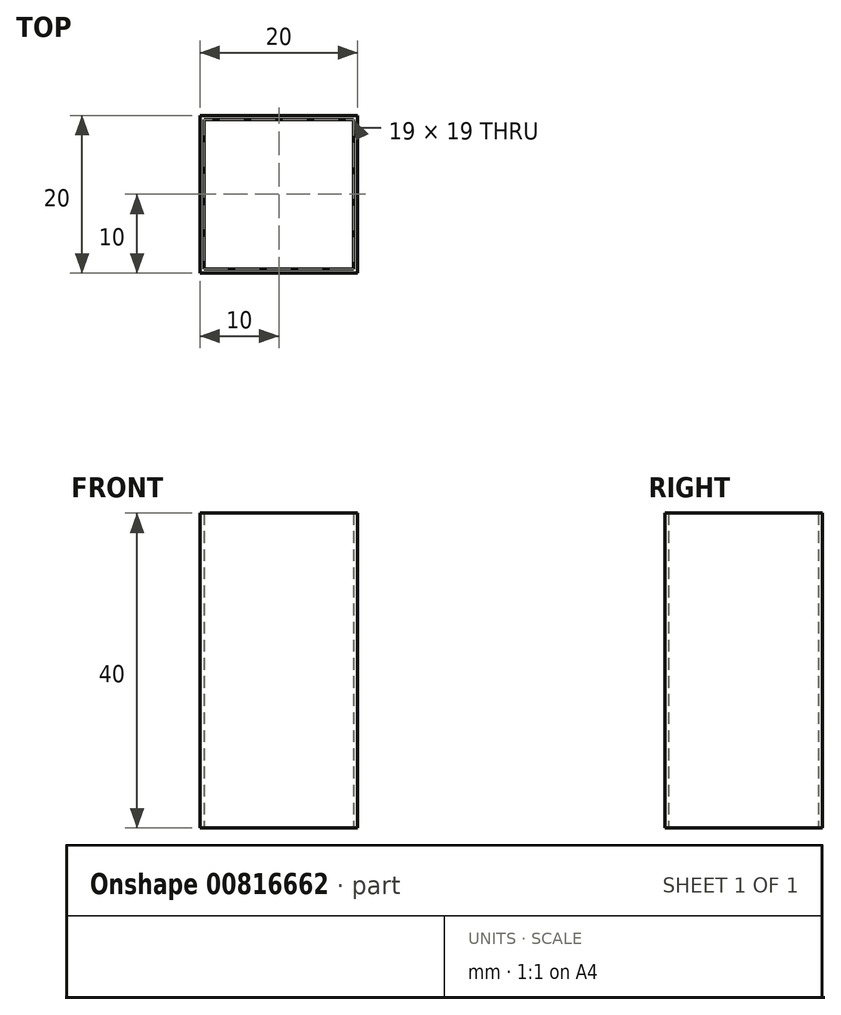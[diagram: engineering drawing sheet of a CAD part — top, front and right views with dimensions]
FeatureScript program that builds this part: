
annotation { "Feature Type Name" : "Feature", "Feature Type Description" : "" }
export const myFeature = defineFeature(function(context is Context, id is Id, definition is map)
    precondition{}
    {
        {
            var Q0;
            Q0=qCreatedBy(makeId("Top.planeOp"),FACE);
            var sketch = newSketch(context, id + "F0", { "sketchPlane" : qUnion([Q0])});
            skLineSegment(sketch, "E0.bottom", {"start": v(10, 10) * mm, "end": v(-10, 10) * mm});
            skLineSegment(sketch, "E0.top", {"start": v(10, -10) * mm, "end": v(-10, -10) * mm});
            skLineSegment(sketch, "E0.left", {"start": v(10, 10) * mm, "end": v(10, -10) * mm});
            skLineSegment(sketch, "E0.right", {"start": v(-10, 10) * mm, "end": v(-10, -10) * mm});
            skPoint(sketch, "E0.middle", {"position": v(0, 0) * mm});
            skLineSegment(sketch, "E1.bottom", {"start": v(9.5, 9.5) * mm, "end": v(-9.5, 9.5) * mm});
            skLineSegment(sketch, "E1.top", {"start": v(9.5, -9.5) * mm, "end": v(-9.5, -9.5) * mm});
            skLineSegment(sketch, "E1.left", {"start": v(9.5, 9.5) * mm, "end": v(9.5, -9.5) * mm});
            skLineSegment(sketch, "E1.right", {"start": v(-9.5, 9.5) * mm, "end": v(-9.5, -9.5) * mm});
            skSolve(sketch);
        }
        {
            var Q0;
            Q0 = qSketchRegion(id + "F0", true);
            extrude(context, id + "F1", {"entities" : qUnion([Q0]), "depth" : 40 * mm, "offsetDistance" : 25 * mm});
        }
    });
